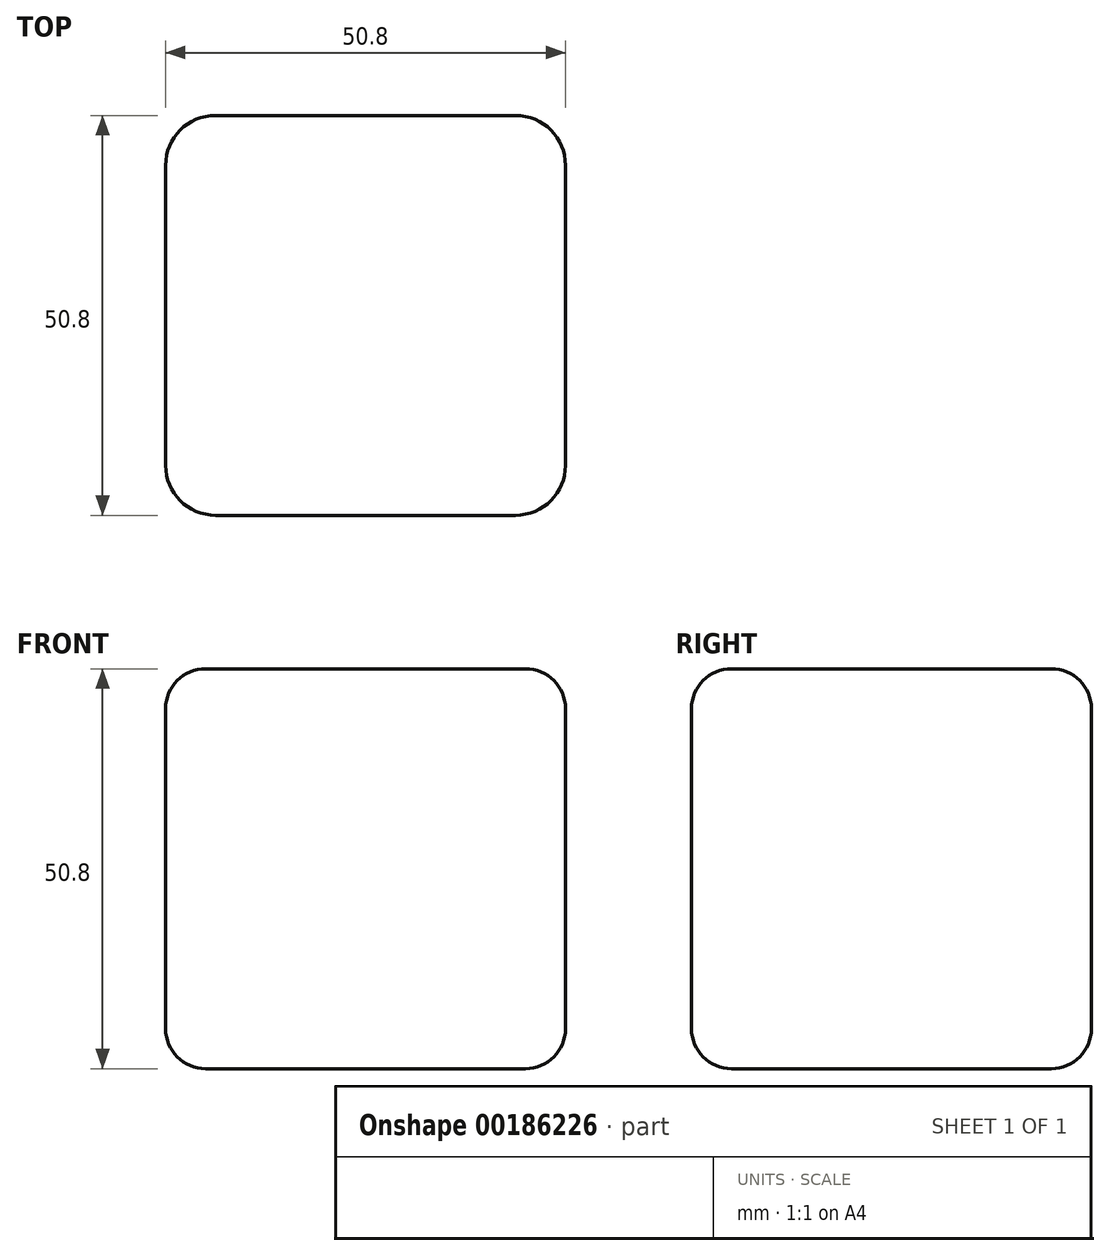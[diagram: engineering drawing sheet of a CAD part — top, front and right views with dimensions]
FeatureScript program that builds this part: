
annotation { "Feature Type Name" : "Feature", "Feature Type Description" : "" }
export const myFeature = defineFeature(function(context is Context, id is Id, definition is map)
    precondition{}
    {
        {
            var Q0;
            Q0=qCreatedBy(makeId("Top.planeOp"),FACE);
            var sketch = newSketch(context, id + "F0", { "sketchPlane" : qUnion([Q0])});
            skLineSegment(sketch, "E0.bottom", {"start": v(-37.73, 24.64) * mm, "end": v(0.37, 24.64) * mm});
            skLineSegment(sketch, "E0.top", {"start": v(-37.73, -26.16) * mm, "end": v(0.37, -26.16) * mm});
            skLineSegment(sketch, "E0.left", {"start": v(-44.08, 18.29) * mm, "end": v(-44.08, -19.81) * mm});
            skLineSegment(sketch, "E0.right", {"start": v(6.72, 18.29) * mm, "end": v(6.72, -19.81) * mm});
            skPoint(sketch, "E1.visualSharp", {"position": v(-44.08, 24.64) * mm});
            skArc(sketch, "E1.filletArc", {"start": v(-37.73, 24.64) * mm, "mid": v(-42.22, 22.78) * mm, "end": v(-44.08, 18.29) * mm});
            skPoint(sketch, "E2.visualSharp", {"position": v(6.72, 24.64) * mm});
            skArc(sketch, "E2.filletArc", {"start": v(6.72, 18.29) * mm, "mid": v(4.86, 22.78) * mm, "end": v(0.37, 24.64) * mm});
            skPoint(sketch, "E3.visualSharp", {"position": v(6.72, -26.16) * mm});
            skArc(sketch, "E3.filletArc", {"start": v(0.37, -26.16) * mm, "mid": v(4.86, -24.3) * mm, "end": v(6.72, -19.81) * mm});
            skPoint(sketch, "E4.visualSharp", {"position": v(-44.08, -26.16) * mm});
            skArc(sketch, "E4.filletArc", {"start": v(-44.08, -19.81) * mm, "mid": v(-42.22, -24.3) * mm, "end": v(-37.73, -26.16) * mm});
            skSolve(sketch);
        }
        {
            var Q0;
            Q0=makeQuery(id+"F0.imprint","IMPRINT",FACE,{"disambiguationData":[TD([[makeQuery(id+"F0.imprint","IMPRINT",EDGE,{"derivedFrom":sQuery(id+"F0.wireOp",EDGE,"E0.bottom")}),-1.0]])]});
            extrude(context, id + "F1", {"entities" : qUnion([Q0]), "depth" : 50.8 * mm});
        }
        {
            var Q0;
            Q0=makeQuery(id+"F1.opExtrude","CAP_EDGE",EDGE,{"disambiguationData":[OSD([sQuery(id+"F0.wireOp",EDGE,"E0.top")])],"isStart":false});
            var Q1;
            Q1=makeQuery(id+"F1.opExtrude","CAP_EDGE",EDGE,{"disambiguationData":[OSD([sQuery(id+"F0.wireOp",EDGE,"E0.top")])],"isStart":true});
            fillet(context, id + "F2", {"entities" : qUnion([Q0, Q1]), "radius" : 5.08 * mm, "tangentPropagation" : true, "allowEdgeOverflow" : false});
        }
    });
